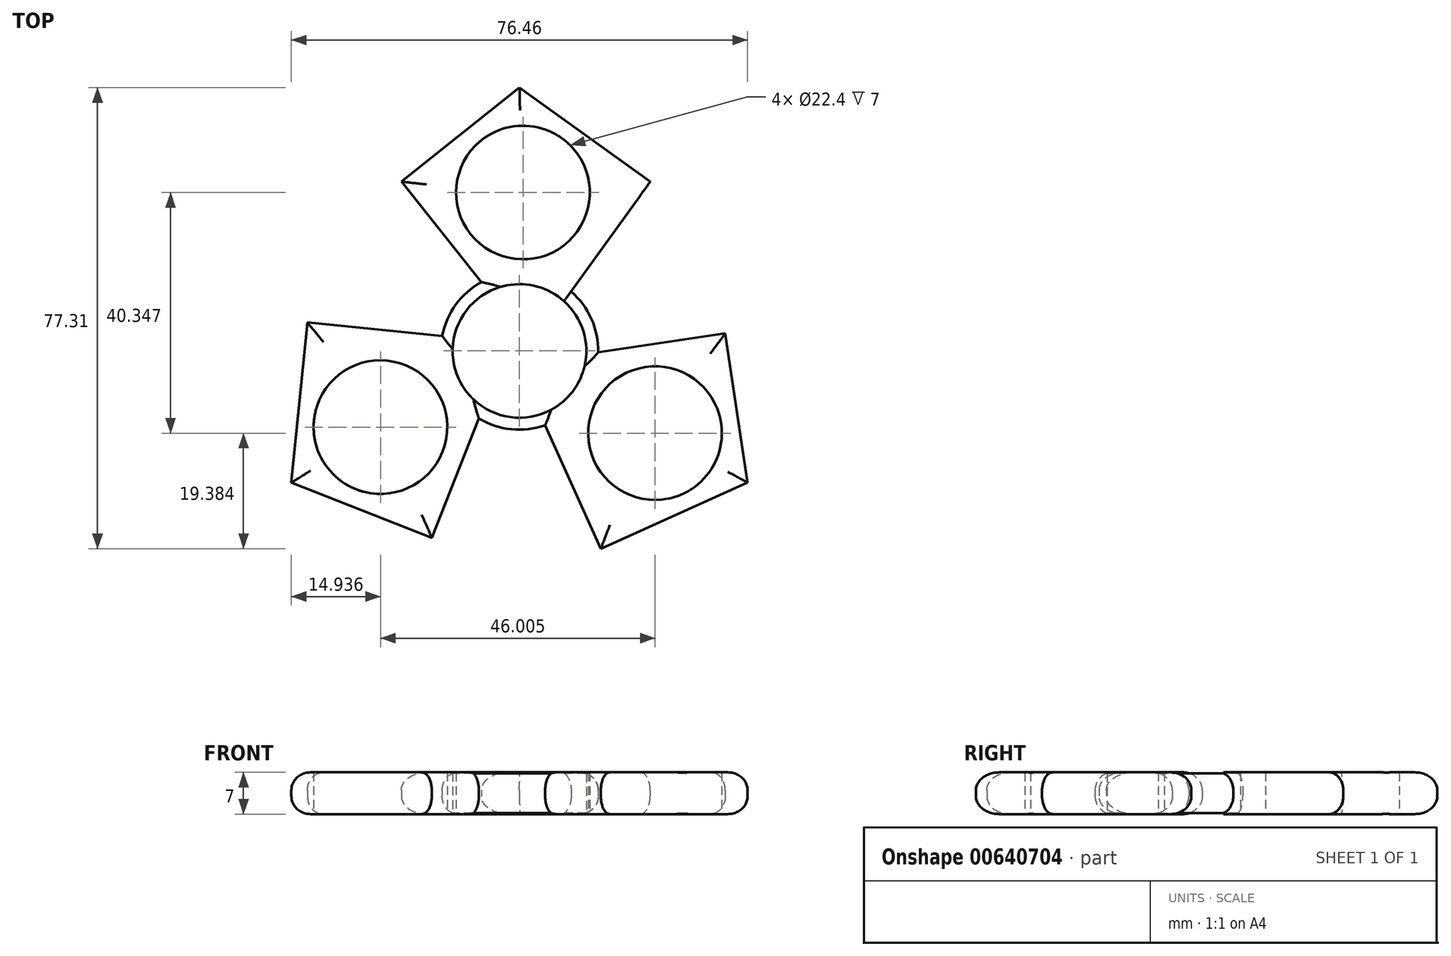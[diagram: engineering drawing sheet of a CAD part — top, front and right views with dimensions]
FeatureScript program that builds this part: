
annotation { "Feature Type Name" : "Feature", "Feature Type Description" : "" }
export const myFeature = defineFeature(function(context is Context, id is Id, definition is map)
    precondition{}
    {
        {
            var Q0;
            Q0=qCreatedBy(makeId("Top.planeOp"),FACE);
            var sketch = newSketch(context, id + "F0", { "sketchPlane" : qUnion([Q0])});
            skCircle(sketch, "E0", {"center": v(0, 0) * mm, "radius": 11.2 * mm});
            skArc(sketch, "E1", {"start": v(13.2, -0.24) * mm, "mid": v(12.06, 5.36) * mm, "end": v(8.66, 9.96) * mm});
            skCircle(sketch, "E2.1.0", {"center": v(-23.3, -12.77) * mm, "radius": 11.2 * mm});
            skLineSegment(sketch, "E3", {"start": v(0, 44.14) * mm, "end": v(21.9, 28.4) * mm});
            skLineSegment(sketch, "E4", {"start": v(21.9, 28.4) * mm, "end": v(8.66, 9.96) * mm});
            skLineSegment(sketch, "E5", {"start": v(8.66, 9.96) * mm, "end": v(21.9, 28.4) * mm});
            skLineSegment(sketch, "E6", {"start": v(0, 44.14) * mm, "end": v(-19.8, 28.4) * mm});
            skLineSegment(sketch, "E7", {"start": v(-19.8, 28.4) * mm, "end": v(-6.39, 11.55) * mm});
            skLineSegment(sketch, "E8.1.0", {"start": v(-38.23, -22.07) * mm, "end": v(-14.7, -31.34) * mm});
            skLineSegment(sketch, "E8.1.1", {"start": v(-14.7, -31.34) * mm, "end": v(-6.8, -11.3) * mm});
            skLineSegment(sketch, "E8.1.2", {"start": v(-12.96, 2.52) * mm, "end": v(-35.54, 4.78) * mm});
            skLineSegment(sketch, "E8.1.3", {"start": v(-38.23, -22.07) * mm, "end": v(-35.54, 4.78) * mm});
            skLineSegment(sketch, "E8.2.0", {"start": v(38.23, -22.07) * mm, "end": v(34.48, 2.94) * mm});
            skLineSegment(sketch, "E8.2.1", {"start": v(34.48, 2.94) * mm, "end": v(13.2, -0.24) * mm});
            skLineSegment(sketch, "E8.2.2", {"start": v(4.3, -12.48) * mm, "end": v(13.63, -33.17) * mm});
            skLineSegment(sketch, "E8.2.3", {"start": v(38.23, -22.07) * mm, "end": v(13.63, -33.17) * mm});
            skCircle(sketch, "E9.1.0", {"center": v(22.71, -13.79) * mm, "radius": 11.2 * mm});
            skCircle(sketch, "E9.2.0", {"center": v(0.58, 26.56) * mm, "radius": 11.2 * mm});
            skArc(sketch, "E10.trimOffspring", {"start": v(-6.8, -11.3) * mm, "mid": v(-1.39, -13.13) * mm, "end": v(4.3, -12.48) * mm});
            skArc(sketch, "E11.trimOffspring", {"start": v(-6.39, 11.55) * mm, "mid": v(-10.68, 7.76) * mm, "end": v(-12.96, 2.52) * mm});
            skSolve(sketch);
        }
        {
            var Q0;
            Q0 = qSketchRegion(id + "F0", true);
            extrude(context, id + "F1", {"entities" : qUnion([Q0]), "depth" : 7 * mm, "offsetDistance" : 25 * mm});
        }
        {
            var Q0;
            Q0=makeQuery(id+"F1.opExtrude","CAP_EDGE",EDGE,{"disambiguationData":[OSD([sQuery(id+"F0.wireOp",EDGE,"E3")])],"isStart":false});
            var Q1;
            Q1=makeQuery(id+"F1.opExtrude","CAP_EDGE",EDGE,{"disambiguationData":[OSD([sQuery(id+"F0.wireOp",EDGE,"E5")])],"isStart":false});
            var Q2;
            Q2=makeQuery(id+"F1.opExtrude","CAP_EDGE",EDGE,{"disambiguationData":[OSD([sQuery(id+"F0.wireOp",EDGE,"E1")])],"isStart":false});
            var Q3;
            Q3=makeQuery(id+"F1.opExtrude","CAP_EDGE",EDGE,{"disambiguationData":[OSD([sQuery(id+"F0.wireOp",EDGE,"E8.2.1")])],"isStart":false});
            var Q4;
            Q4=makeQuery(id+"F1.opExtrude","CAP_EDGE",EDGE,{"disambiguationData":[OSD([sQuery(id+"F0.wireOp",EDGE,"E8.2.0")])],"isStart":false});
            var Q5;
            Q5=makeQuery(id+"F1.opExtrude","CAP_EDGE",EDGE,{"disambiguationData":[OSD([sQuery(id+"F0.wireOp",EDGE,"E8.2.3")])],"isStart":false});
            var Q6;
            Q6=makeQuery(id+"F1.opExtrude","CAP_EDGE",EDGE,{"disambiguationData":[OSD([sQuery(id+"F0.wireOp",EDGE,"E8.2.2")])],"isStart":false});
            var Q7;
            Q7=makeQuery(id+"F1.opExtrude","CAP_EDGE",EDGE,{"disambiguationData":[OSD([sQuery(id+"F0.wireOp",EDGE,"E10.trimOffspring")])],"isStart":false});
            var Q8;
            Q8=makeQuery(id+"F1.opExtrude","CAP_EDGE",EDGE,{"disambiguationData":[OSD([sQuery(id+"F0.wireOp",EDGE,"E8.1.1")])],"isStart":false});
            var Q9;
            Q9=makeQuery(id+"F1.opExtrude","CAP_EDGE",EDGE,{"disambiguationData":[OSD([sQuery(id+"F0.wireOp",EDGE,"E8.1.0")])],"isStart":false});
            var Q10;
            Q10=makeQuery(id+"F1.opExtrude","CAP_EDGE",EDGE,{"disambiguationData":[OSD([sQuery(id+"F0.wireOp",EDGE,"E8.1.3")])],"isStart":false});
            var Q11;
            Q11=makeQuery(id+"F1.opExtrude","CAP_EDGE",EDGE,{"disambiguationData":[OSD([sQuery(id+"F0.wireOp",EDGE,"E7")])],"isStart":false});
            var Q12;
            Q12=makeQuery(id+"F1.opExtrude","CAP_EDGE",EDGE,{"disambiguationData":[OSD([sQuery(id+"F0.wireOp",EDGE,"E6")])],"isStart":false});
            var Q13;
            Q13=makeQuery(id+"F1.opExtrude","CAP_EDGE",EDGE,{"disambiguationData":[OSD([sQuery(id+"F0.wireOp",EDGE,"E8.1.2")])],"isStart":false});
            var Q14;
            Q14=makeQuery(id+"F1.opExtrude","CAP_EDGE",EDGE,{"disambiguationData":[OSD([sQuery(id+"F0.wireOp",EDGE,"E11.trimOffspring")])],"isStart":false});
            fillet(context, id + "F2", {"entities" : qUnion([Q0, Q1, Q2, Q3, Q4, Q5, Q6, Q7, Q8, Q9, Q10, Q11, Q12, Q13, Q14]), "radius" : 3 * mm, "tangentPropagation" : true, "allowEdgeOverflow" : false});
        }
        {
            var Q0;
            Q0=makeQuery(id+"F1.opExtrude","CAP_EDGE",EDGE,{"disambiguationData":[OSD([sQuery(id+"F0.wireOp",EDGE,"E6")])],"isStart":true});
            var Q1;
            Q1=makeQuery(id+"F1.opExtrude","CAP_EDGE",EDGE,{"disambiguationData":[OSD([sQuery(id+"F0.wireOp",EDGE,"E3")])],"isStart":true});
            var Q2;
            Q2=makeQuery(id+"F1.opExtrude","CAP_EDGE",EDGE,{"disambiguationData":[OSD([sQuery(id+"F0.wireOp",EDGE,"E5")])],"isStart":true});
            var Q3;
            Q3=makeQuery(id+"F1.opExtrude","CAP_EDGE",EDGE,{"disambiguationData":[OSD([sQuery(id+"F0.wireOp",EDGE,"E8.2.1")])],"isStart":true});
            var Q4;
            Q4=makeQuery(id+"F1.opExtrude","CAP_EDGE",EDGE,{"disambiguationData":[OSD([sQuery(id+"F0.wireOp",EDGE,"E1")])],"isStart":true});
            var Q5;
            Q5=makeQuery(id+"F1.opExtrude","CAP_EDGE",EDGE,{"disambiguationData":[OSD([sQuery(id+"F0.wireOp",EDGE,"E8.2.0")])],"isStart":true});
            var Q6;
            Q6=makeQuery(id+"F1.opExtrude","CAP_EDGE",EDGE,{"disambiguationData":[OSD([sQuery(id+"F0.wireOp",EDGE,"E8.2.3")])],"isStart":true});
            var Q7;
            Q7=makeQuery(id+"F1.opExtrude","CAP_EDGE",EDGE,{"disambiguationData":[OSD([sQuery(id+"F0.wireOp",EDGE,"E8.2.2")])],"isStart":true});
            var Q8;
            Q8=makeQuery(id+"F1.opExtrude","CAP_EDGE",EDGE,{"disambiguationData":[OSD([sQuery(id+"F0.wireOp",EDGE,"E10.trimOffspring")])],"isStart":true});
            var Q9;
            Q9=makeQuery(id+"F1.opExtrude","CAP_EDGE",EDGE,{"disambiguationData":[OSD([sQuery(id+"F0.wireOp",EDGE,"E8.1.1")])],"isStart":true});
            var Q10;
            Q10=makeQuery(id+"F1.opExtrude","CAP_EDGE",EDGE,{"disambiguationData":[OSD([sQuery(id+"F0.wireOp",EDGE,"E8.1.0")])],"isStart":true});
            var Q11;
            Q11=makeQuery(id+"F1.opExtrude","CAP_EDGE",EDGE,{"disambiguationData":[OSD([sQuery(id+"F0.wireOp",EDGE,"E8.1.3")])],"isStart":true});
            var Q12;
            Q12=makeQuery(id+"F1.opExtrude","CAP_EDGE",EDGE,{"disambiguationData":[OSD([sQuery(id+"F0.wireOp",EDGE,"E8.1.2")])],"isStart":true});
            var Q13;
            Q13=makeQuery(id+"F1.opExtrude","CAP_EDGE",EDGE,{"disambiguationData":[OSD([sQuery(id+"F0.wireOp",EDGE,"E11.trimOffspring")])],"isStart":true});
            var Q14;
            Q14=makeQuery(id+"F1.opExtrude","CAP_EDGE",EDGE,{"disambiguationData":[OSD([sQuery(id+"F0.wireOp",EDGE,"E7")])],"isStart":true});
            fillet(context, id + "F3", {"entities" : qUnion([Q0, Q1, Q2, Q3, Q4, Q5, Q6, Q7, Q8, Q9, Q10, Q11, Q12, Q13, Q14]), "radius" : 3 * mm, "tangentPropagation" : true, "allowEdgeOverflow" : false});
        }
    });
